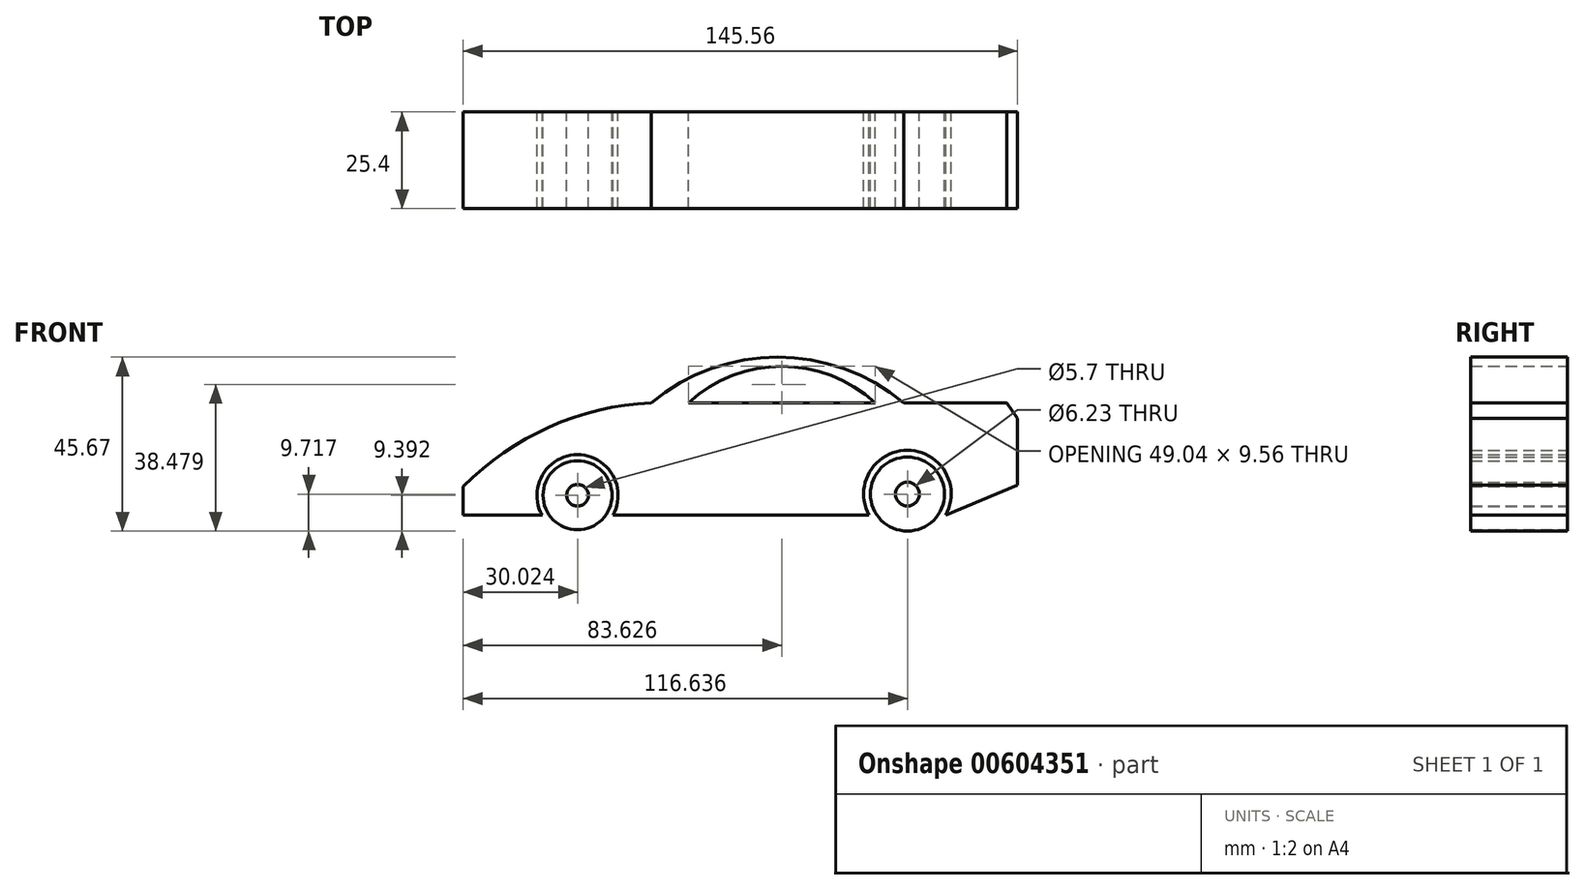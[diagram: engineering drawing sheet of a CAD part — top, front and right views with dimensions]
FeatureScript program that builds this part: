
annotation { "Feature Type Name" : "Feature", "Feature Type Description" : "" }
export const myFeature = defineFeature(function(context is Context, id is Id, definition is map)
    precondition{}
    {
        {
            var Q0;
            Q0=qCreatedBy(makeId("Front.planeOp"),FACE);
            var sketch = newSketch(context, id + "F0", { "sketchPlane" : qUnion([Q0])});
            skArc(sketch, "E0", {"start": v(-33.18, -29.55) * mm, "mid": v(-42.46, -13.65) * mm, "end": v(-51.73, -29.55) * mm});
            skLineSegment(sketch, "E1", {"start": v(-51.73, -29.55) * mm, "end": v(-72.48, -29.55) * mm});
            skLineSegment(sketch, "E2", {"start": v(-72.48, -22) * mm, "end": v(-72.48, -29.55) * mm});
            skArc(sketch, "E3", {"start": v(-23.12, 0) * mm, "mid": v(-49.86, -6.38) * mm, "end": v(-72.48, -22) * mm});
            skArc(sketch, "E4", {"start": v(43.21, 0) * mm, "mid": v(10.05, 11.97) * mm, "end": v(-23.12, 0) * mm});
            skLineSegment(sketch, "E5", {"start": v(43.21, 0) * mm, "end": v(51.39, 0) * mm});
            skLineSegment(sketch, "E6", {"start": v(70.25, 0) * mm, "end": v(43.21, 0) * mm});
            skLineSegment(sketch, "E7", {"start": v(70.25, 0) * mm, "end": v(73.08, -4.09) * mm});
            skLineSegment(sketch, "E8", {"start": v(73.08, -4.09) * mm, "end": v(73.08, -8.8) * mm});
            skLineSegment(sketch, "E9", {"start": v(73.08, -8.8) * mm, "end": v(73.08, -21.7) * mm});
            skLineSegment(sketch, "E10", {"start": v(73.08, -21.7) * mm, "end": v(54.22, -29.55) * mm});
            skArc(sketch, "E11", {"start": v(54.22, -29.55) * mm, "mid": v(44.16, -12.48) * mm, "end": v(34.1, -29.55) * mm});
            skLineSegment(sketch, "E12", {"start": v(-33.18, -29.55) * mm, "end": v(34.1, -29.55) * mm});
            skCircle(sketch, "E13", {"center": v(-42.46, -24.3) * mm, "radius": 9.07 * mm});
            skCircle(sketch, "E14", {"center": v(44.16, -23.98) * mm, "radius": 9.72 * mm});
            skArc(sketch, "E15", {"start": v(35.67, 0) * mm, "mid": v(11.15, 9.56) * mm, "end": v(-13.38, 0) * mm});
            skLineSegment(sketch, "E16", {"start": v(-13.38, 0) * mm, "end": v(35.67, 0) * mm});
            skCircle(sketch, "E17", {"center": v(44.16, -23.98) * mm, "radius": 3.12 * mm});
            skCircle(sketch, "E18", {"center": v(-42.46, -24.3) * mm, "radius": 2.85 * mm});
            skSolve(sketch);
        }
        {
            var Q0;
            Q0 = qSketchRegion(id + "F0", true);
            extrude(context, id + "F1", {"entities" : qUnion([Q0]), "depth" : 25.4 * mm, "offsetDistance" : 25.4 * mm});
        }
    });
